# Revit family: LBWD - FILTER BOX
name_source: partatom
category: Plumbing Fixtures
units: mm (PartAtom-declared; Revit-internal decimal feet)

## family parameters
Cut with Voids When Loaded = No
Host = Face
Part Type = Normal
Room Calculation Point = No
Round Connector Dimension = Use Diameter
Shared = No

## types (4) — shared parameters
ACTIVATION BY = ELECTRONIC BOTTLE FILLER SENSOR
CHILLING OPTION = NON-REFRIGERATED
CW Connection = No
DIMENSIONS = 5-1/8" x 18" x 28"
DRAIN = 1 1/4"
Default Elevation = 3' - 11"
FILTER BOX = LBWD FILTER BOX
HW Connection = No
INSTALLATION LOCATION = INDOOR
NO OF STATIONS SERVED = 1
POWER = 115V/60Hz
RATED WATTS = 25
Vent Connection = No
WATER INLET = 3/8"
Waste Connection = No

## per-type parameters (varying)
| type | APPROX SHIPPING WEIGHT | FACE FINISH | FINISH | MOUNTING TYPE |
| LBWD00BKC | 40 LBS | LBWD BLACK | MIDNIGHT BLACK | BUILT-IN |
| LBWD00WHC | 40 LBS | LBWD WHITE | ASPEN WHITE | BUILT-IN |
| LBWDC00BKC | 41 LBS | LBWD BLACK | MIDNIGHT BLACK | WALL MOUNT |
| LBWDC00WHC | 41 LBS | LBWD WHITE | ASPEN WHITE | WALL MOUNT |

## geometry (parser evidence)
native form markers: Sweep x13
no freeform markers — native parametric forms only
